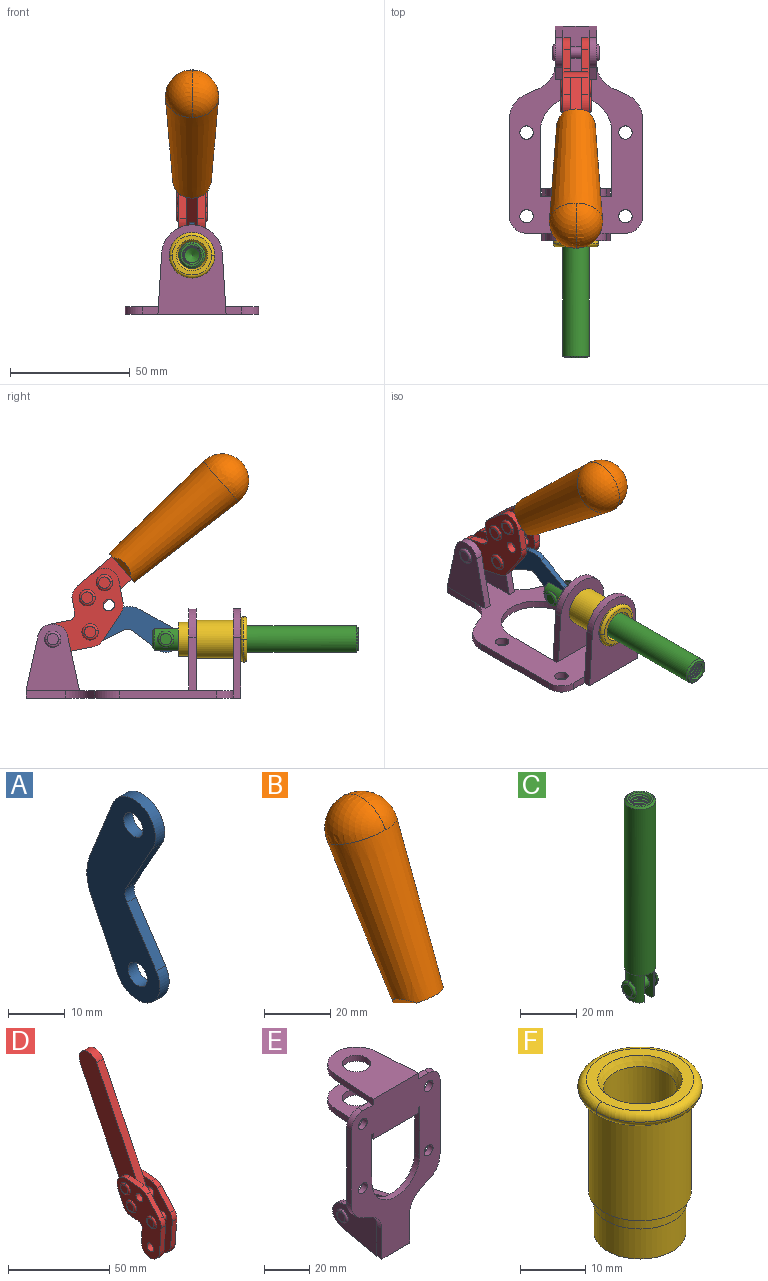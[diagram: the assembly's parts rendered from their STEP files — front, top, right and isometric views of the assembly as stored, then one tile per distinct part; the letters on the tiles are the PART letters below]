
ASSEMBLY  parts=6 mates=6
PART A: 12 faces, bbox 2.3x18.2x42.8 mm
  f0: cylinder r=2.4mm len=4.8mm, axis (1,0,0), area 34.9mm2, adj f4,f11
  f1: cylinder r=10.41mm len=8.47mm, axis (1,0,0), area 20.2mm2, adj f4,f9,f10,f11
  f2: cylinder r=3.05mm len=3.16mm, axis (1,0,0), area 7.7mm2, adj f4,f6,f7,f11
  f3: cylinder r=2.4mm len=4.8mm, axis (1,0,0), area 34.9mm2, adj f4,f11
  f4: plane 42.81x18.23mm, normal (-1,0,0), area 414.1mm2, adj f0,f1,f2,f3,f5,f6,f7,f8
  f5: cylinder r=5.54mm len=10.67mm, axis (1,0,0), area 41.8mm2, adj f4,f6,f10,f11
  f6: plane 11.66x6.53mm, normal (0,-0.87,-0.49), area 30.9mm2, adj f2,f4,f5,f11
  f7: plane 11.17x7.33mm, normal (0,-0.84,0.55), area 30.9mm2, adj f2,f4,f8,f11
  f8: cylinder r=5.54mm len=10.51mm, axis (1,0,0), area 41.8mm2, adj f4,f7,f9,f11
  f9: plane 13.67x6.67mm, normal (0,0.9,-0.44), area 35.1mm2, adj f1,f4,f8,f11
  f10: plane 14.1x5.7mm, normal (0,0.93,0.37), area 35.1mm2, adj f1,f4,f5,f11
  f11: plane 42.81x18.23mm, normal (1,0,0), area 414.1mm2, adj f0,f1,f2,f3,f5,f6,f7,f8
PART B: 11 faces, bbox 22.3x42.6x64.5 mm
  f0: sphere r=11.13mm, area 411.4mm2, adj f1,f8
  f1: cone r=11.11mm half-angle=3.3deg, axis (0,0.44,0.9), area 3251.8mm2, adj f0,f7,f8,f9,f10
  f2: cylinder r=6.16mm len=11.7mm, axis (1,0,0), area 89.5mm2, adj f3,f4,f5,f6
  f3: plane 60.23x36.75mm, normal (-1,0,0), area 763.6mm2, adj f2,f4,f6,f10
  f4: plane 51.37x25.05mm, normal (0,0.9,-0.44), area 264.2mm2, adj f2,f3,f5,f10
  f5: plane 60.23x36.75mm, normal (1,0,0), area 763.6mm2, adj f2,f4,f6,f10
  f6: plane 51.37x25.05mm, normal (0,-0.9,0.44), area 264.2mm2, adj f2,f3,f5,f10
  f7: plane 9.95x5.95mm, normal (0.71,-0.31,-0.64), area 25.8mm2, adj f1,f10
  f8: sphere r=11.13mm, area 411.4mm2, adj f0,f1
  f9: plane 9.95x5.95mm, normal (-0.71,-0.31,-0.64), area 25.8mm2, adj f1,f10
  f10: plane 14.27x11.38mm, normal (0,-0.44,-0.9), area 106.7mm2, adj f1,f3,f4,f5,f6,f7,f9
PART C: 48 faces, bbox 12.6x11.1x86.1 mm
  f0: torus R=2.41mm, axis (-1,0,0), area 15mm2, adj f30,f32,f34
  f1: torus R=2.41mm, axis (-1,0,0), area 15mm2, adj f29,f31,f33
  f2: cylinder r=5.54mm len=72.39mm, axis (0,0,1), area 2518.5mm2, adj f3,f4,f42,f43
  f3: cone r=5.54mm half-angle=45deg, axis (0,0,1), area 7.6mm2, adj f2,f5,f41
  f4: cone r=5.54mm half-angle=45deg, axis (0,0,-1), area 34.9mm2, adj f2,f39
  f5: cylinder r=5.08mm len=11.48mm, axis (0,0,1), area 108.3mm2, adj f3,f7,f8,f41
  f6: cylinder r=2.41mm len=4.83mm, axis (-1,0,0), area 71.2mm2, adj f40,f41
  f7: cylinder r=2.41mm len=4.83mm, axis (-1,0,0), area 7.6mm2, adj f5,f34
  f8: cone r=5.08mm half-angle=45deg, axis (0,0,1), area 10.6mm2, adj f5,f37,f41
  f9: cone r=3.98mm half-angle=45deg, axis (0,0,1), area 17.6mm2, adj f27,f39,f45,f46,f47
  f10: cylinder r=2.41mm len=4.83mm, axis (-1,0,0), area 7.6mm2, adj f33,f38
  f11: cylinder r=3.2mm len=6.4mm, axis (0,0,1), area 78.4mm2, adj f12,f28,f44,f45,f47
  f12: cylinder r=3.2mm len=6.4mm, axis (0,0,1), area 10.5mm2, adj f11,f13,f45,f47
  f13: cylinder r=3.2mm len=6.4mm, axis (0,0,1), area 10.5mm2, adj f12,f14,f45,f47
  f14: cylinder r=3.2mm len=6.4mm, axis (0,0,1), area 10.5mm2, adj f13,f15,f45,f47
  f15: cylinder r=3.2mm len=6.4mm, axis (0,0,1), area 10.5mm2, adj f14,f16,f45,f47
  f16: cylinder r=3.2mm len=6.4mm, axis (0,0,1), area 10.5mm2, adj f15,f17,f45,f47
  f17: cylinder r=3.2mm len=6.4mm, axis (0,0,1), area 10.5mm2, adj f16,f18,f45,f47
  f18: cylinder r=3.2mm len=6.4mm, axis (0,0,1), area 10.5mm2, adj f17,f19,f45,f47
  f19: cylinder r=3.2mm len=6.4mm, axis (0,0,1), area 10.5mm2, adj f18,f20,f45,f47
  f20: cylinder r=3.2mm len=6.4mm, axis (0,0,1), area 10.5mm2, adj f19,f21,f45,f47
  f21: cylinder r=3.2mm len=6.4mm, axis (0,0,1), area 10.5mm2, adj f20,f22,f45,f47
  f22: cylinder r=3.2mm len=6.4mm, axis (0,0,1), area 10.5mm2, adj f21,f23,f45,f47
  f23: cylinder r=3.2mm len=6.4mm, axis (0,0,1), area 10.5mm2, adj f22,f24,f45,f47
  f24: cylinder r=3.2mm len=6.4mm, axis (0,0,1), area 10.5mm2, adj f23,f25,f45,f47
  f25: cylinder r=3.2mm len=6.4mm, axis (0,0,1), area 10.5mm2, adj f24,f26,f45,f47
  f26: cylinder r=3.2mm len=6.4mm, axis (0,0,1), area 10.5mm2, adj f25,f27,f45,f47
  f27: cylinder r=3.2mm len=6.4mm, axis (0,0,1), area 7.4mm2, adj f9,f26,f45,f47
  f28: cone r=3.2mm half-angle=60deg, axis (0,0,1), area 37.2mm2, adj f11
  f29: plane 4.83x4.83mm, normal (-1,0,0), area 18.3mm2, adj f1,f31
  f30: plane 4.83x4.83mm, normal (1,0,0), area 18.3mm2, adj f0,f32
  f31: torus R=2.41mm, axis (-1,0,0), area 15mm2, adj f1,f29,f33
  f32: torus R=2.41mm, axis (-1,0,0), area 15mm2, adj f0,f30,f34
  f33: plane 6.83x6.83mm, normal (1,0,0), area 18.3mm2, adj f1,f10,f31
  f34: plane 6.83x6.83mm, normal (-1,0,0), area 18.3mm2, adj f0,f7,f32
  f35: cone r=5.08mm half-angle=45deg, axis (0,0,1), area 10.6mm2, adj f36,f38,f40
  f36: plane 7.25x1.97mm, normal (0,0,-1), area 10mm2, adj f35,f40
  f37: plane 7.25x1.97mm, normal (0,0,-1), area 10mm2, adj f8,f41
  f38: cylinder r=5.08mm len=11.48mm, axis (0,0,1), area 108.3mm2, adj f10,f35,f40,f42
  f39: plane 9.55x9.55mm, normal (0,0,1), area 22mm2, adj f4,f9
  f40: plane 12.76x10.09mm, normal (1,0,0), area 95.7mm2, adj f6,f35,f36,f38,f42,f43
  f41: plane 12.76x10.09mm, normal (-1,0,0), area 95.7mm2, adj f3,f5,f6,f8,f37,f43
  f42: cone r=5.54mm half-angle=45deg, axis (0,0,1), area 7.6mm2, adj f2,f38,f40
  f43: plane 11.07x4.7mm, normal (0,0,-1), area 50.4mm2, adj f2,f40,f41
  f44: plane 0.89x0.62mm, normal (-1,0,0), area 0.3mm2, adj f11,f45,f46,f47
  f45: bspline ~24.8x7.63mm, area 266.6mm2, adj f9,f11,f12,f13,f14,f15,f16,f17
  f46: bspline ~24.87x7.63mm, area 73.6mm2, adj f9,f44,f45,f47
  f47: bspline ~24.98x7.63mm, area 272.5mm2, adj f9,f11,f12,f13,f14,f15,f16,f17
PART D: 59 faces, bbox 12.9x60.2x99.6 mm
  f0: torus R=2.39mm, axis (-1,0,0), area 14.9mm2, adj f20,f43,f51
  f1: torus R=2.39mm, axis (-1,0,0), area 14.9mm2, adj f19,f42,f51
  f2: torus R=2.39mm, axis (-1,0,0), area 14.9mm2, adj f18,f35,f51
  f3: torus R=2.39mm, axis (-1,0,0), area 14.9mm2, adj f14,f17,f23
  f4: torus R=2.39mm, axis (-1,0,0), area 14.9mm2, adj f13,f16,f23
  f5: torus R=2.39mm, axis (-1,0,0), area 14.9mm2, adj f12,f15,f23
  f6: cylinder r=2.39mm len=4.78mm, axis (1,0,0), area 46.5mm2, adj f48,f50,f51
  f7: cylinder r=2.39mm len=4.78mm, axis (1,0,0), area 46.5mm2, adj f50,f51
  f8: cylinder r=6.35mm len=12.68mm, axis (1,0,0), area 61.8mm2, adj f38,f39,f50,f51
  f9: cylinder r=2.39mm len=4.78mm, axis (-1,0,0), area 70.5mm2, adj f46,f50
  f10: cylinder r=2.39mm len=4.78mm, axis (-1,0,0), area 46.5mm2, adj f23,f45,f46
  f11: cylinder r=2.39mm len=4.78mm, axis (-1,0,0), area 46.5mm2, adj f23,f46
  f12: plane 4.78x4.78mm, normal (1,0,0), area 17.9mm2, adj f5,f15
  f13: plane 4.78x4.78mm, normal (1,0,0), area 17.9mm2, adj f4,f16
  f14: plane 4.78x4.78mm, normal (1,0,0), area 17.9mm2, adj f3,f17
  f15: torus R=2.39mm, axis (-1,0,0), area 14.9mm2, adj f5,f12,f23
  f16: torus R=2.39mm, axis (-1,0,0), area 14.9mm2, adj f4,f13,f23
  f17: torus R=2.39mm, axis (-1,0,0), area 14.9mm2, adj f3,f14,f23
  f18: plane 4.78x4.78mm, normal (-1,0,0), area 17.9mm2, adj f2,f35
  f19: plane 4.78x4.78mm, normal (-1,0,0), area 17.9mm2, adj f1,f42
  f20: plane 4.78x4.78mm, normal (-1,0,0), area 17.9mm2, adj f0,f43
  f21: plane 2.26x0.2mm, normal (1,0,0), area 0.2mm2, adj f31,f44
  f22: plane 2.26x0.2mm, normal (-1,0,0), area 0.2mm2, adj f41,f44
  f23: plane 39.37x30.77mm, normal (1,0,0), area 565.5mm2, adj f3,f4,f5,f10,f11,f15,f16,f17
  f24: cylinder r=6.1mm len=4.15mm, axis (-1,0,0), area 14.7mm2, adj f23,f25,f32,f46
  f25: plane 10.25x9.01mm, normal (0,-0.75,0.66), area 42.3mm2, adj f23,f24,f26,f46
  f26: cylinder r=6.35mm len=4.64mm, axis (-1,0,0), area 15.6mm2, adj f23,f25,f27,f46
  f27: plane 15.84x3.1mm, normal (0,-1,-0.07), area 49.2mm2, adj f23,f26,f28,f46
  f28: cylinder r=6.35mm len=12.68mm, axis (-1,0,0), area 61.8mm2, adj f23,f27,f29,f46
  f29: plane 8.11x3.1mm, normal (0,1,0.07), area 25.2mm2, adj f23,f28,f30,f46
  f30: cylinder r=3.05mm len=3.25mm, axis (-1,0,0), area 14.8mm2, adj f23,f29,f31,f46
  f31: plane 5.99x3.1mm, normal (0,0.07,-1), area 18.6mm2, adj f21,f23,f30,f44,f46
  f32: plane 9.5x3.1mm, normal (0,-0.07,1), area 29.5mm2, adj f23,f24,f33,f46,f47
  f33: cylinder r=6.1mm len=8.63mm, axis (-1,0,0), area 39.1mm2, adj f23,f32,f34,f47
  f34: plane 8.65x3.96mm, normal (0,0.91,-0.42), area 29.5mm2, adj f23,f33,f44,f47
  f35: torus R=2.39mm, axis (-1,0,0), area 14.9mm2, adj f2,f18,f51
  f36: plane 10.25x9.01mm, normal (0,-0.75,0.66), area 42.3mm2, adj f37,f49,f50,f51
  f37: cylinder r=6.35mm len=4.64mm, axis (1,0,0), area 15.6mm2, adj f36,f38,f50,f51
  f38: plane 15.84x3.1mm, normal (0,-1,-0.07), area 49.2mm2, adj f8,f37,f50,f51
  f39: plane 8.11x3.1mm, normal (0,1,0.07), area 25.2mm2, adj f8,f40,f50,f51
  f40: cylinder r=3.05mm len=3.25mm, axis (1,0,0), area 14.8mm2, adj f39,f41,f50,f51
  f41: plane 5.99x3.1mm, normal (0,0.07,-1), area 18.6mm2, adj f22,f40,f44,f50,f51
  f42: torus R=2.39mm, axis (-1,0,0), area 14.9mm2, adj f1,f19,f51
  f43: torus R=2.39mm, axis (-1,0,0), area 14.9mm2, adj f0,f20,f51
  f44: cylinder r=6.35mm len=12.12mm, axis (-1,0,0), area 128.9mm2, adj f21,f22,f23,f31,f34,f41,f46,f47
  f45: plane 2.65x1.35mm, normal (1,0,0), area 1mm2, adj f10,f55
  f46: plane 39.08x20.42mm, normal (-1,0,0), area 412.5mm2, adj f9,f10,f11,f24,f25,f26,f27,f28
  f47: plane 77.62x39.82mm, normal (1,0,0), area 850mm2, adj f32,f33,f34,f44,f53,f54,f55
  f48: plane 2.65x1.35mm, normal (-1,0,0), area 1mm2, adj f6,f55
  f49: cylinder r=6.1mm len=4.15mm, axis (1,0,0), area 14.7mm2, adj f36,f50,f51,f56
  f50: plane 39.08x20.42mm, normal (1,0,0), area 412.5mm2, adj f6,f7,f8,f9,f36,f37,f38,f39
  f51: plane 39.37x30.77mm, normal (-1,0,0), area 565.5mm2, adj f0,f1,f2,f6,f7,f8,f35,f36
  f52: plane 8.65x3.96mm, normal (0,0.91,-0.42), area 29.5mm2, adj f44,f51,f57,f58
  f53: plane 68.49x33.4mm, normal (0,0.9,-0.44), area 358.1mm2, adj f44,f47,f54,f58
  f54: cylinder r=6.35mm len=12.06mm, axis (1,0,0), area 93.7mm2, adj f47,f53,f55,f58
  f55: plane 68.49x33.4mm, normal (0,-0.9,0.44), area 358.1mm2, adj f44,f45,f46,f47,f48,f50,f54,f58
  f56: plane 9.5x3.1mm, normal (0,-0.07,1), area 29.5mm2, adj f49,f50,f51,f57,f58
  f57: cylinder r=6.1mm len=8.63mm, axis (1,0,0), area 39.1mm2, adj f51,f52,f56,f58
  f58: plane 77.62x39.82mm, normal (-1,0,0), area 850mm2, adj f44,f52,f53,f54,f55,f56,f57
PART E: 55 faces, bbox 55.7x37.4x89.8 mm
  f0: torus R=2.41mm, axis (-1,0,0), area 15mm2, adj f11,f15,f25
  f1: torus R=2.41mm, axis (-1,0,0), area 15mm2, adj f10,f12,f22
  f2: cylinder r=2.78mm len=5.56mm, axis (0,-1,0), area 54.2mm2, adj f30,f54
  f3: cylinder r=14.99mm len=29.97mm, axis (0,-1,0), area 145.9mm2, adj f30,f49,f53,f54
  f4: cylinder r=2.78mm len=5.56mm, axis (0,-1,0), area 54.2mm2, adj f30,f54
  f5: cylinder r=2.78mm len=5.56mm, axis (0,-1,0), area 54.2mm2, adj f30,f54
  f6: cylinder r=2.78mm len=5.56mm, axis (0,-1,0), area 54.2mm2, adj f30,f54
  f7: cylinder r=6.35mm len=12.7mm, axis (0,0,1), area 123.6mm2, adj f27,f51
  f8: cylinder r=6.35mm len=12.7mm, axis (0,0,-1), area 124.7mm2, adj f21,f35
  f9: cylinder r=2.41mm len=11.18mm, axis (-1,0,0), area 169.4mm2, adj f16,f19
  f10: plane 4.83x4.83mm, normal (1,0,0), area 18.3mm2, adj f1,f12
  f11: plane 4.83x4.83mm, normal (-1,0,0), area 18.3mm2, adj f0,f15
  f12: torus R=2.41mm, axis (-1,0,0), area 15mm2, adj f1,f10,f22
  f13: cylinder r=6.35mm len=12.41mm, axis (1,0,0), area 53.4mm2, adj f18,f19,f22,f23
  f14: cylinder r=6.35mm len=12.41mm, axis (-1,0,0), area 53.4mm2, adj f16,f17,f24,f25
  f15: torus R=2.41mm, axis (-1,0,0), area 15mm2, adj f0,f11,f25
  f16: plane 27.86x22.35mm, normal (1,0,0), area 425.4mm2, adj f9,f14,f17,f24,f30
  f17: plane 22.86x4.97mm, normal (0,0.21,0.98), area 72.5mm2, adj f14,f16,f25,f30
  f18: plane 22.86x4.97mm, normal (0,0.21,0.98), area 72.5mm2, adj f13,f19,f22,f30
  f19: plane 27.86x22.35mm, normal (-1,0,0), area 425.4mm2, adj f9,f13,f18,f23,f30
  f20: cylinder r=12.7mm len=25.35mm, axis (0,0,-1), area 119.8mm2, adj f21,f34,f35,f36
  f21: plane 34.21x28.07mm, normal (0,0,-1), area 702.4mm2, adj f8,f20,f30,f34,f36
  f22: plane 27.96x22.45mm, normal (1,0,0), area 407.2mm2, adj f1,f12,f13,f18,f23,f30,f42,f43
  f23: plane 22.86x4.97mm, normal (0,0.21,-0.98), area 72.5mm2, adj f13,f19,f22,f44
  f24: plane 22.86x4.97mm, normal (0,0.21,-0.98), area 72.5mm2, adj f14,f16,f25,f44
  f25: plane 27.86x22.35mm, normal (-1,0,0), area 407.1mm2, adj f0,f14,f15,f17,f24,f30,f45,f46
  f26: plane 3.1x0.95mm, normal (0,0,-1), area 2.7mm2, adj f30,f49,f50,f54
  f27: plane 34.21x28.07mm, normal (0,0,1), area 702.4mm2, adj f7,f28,f30,f50,f52
  f28: cylinder r=12.7mm len=25.35mm, axis (0,0,1), area 118.8mm2, adj f27,f50,f51,f52
  f29: plane 3.1x0.95mm, normal (0,0,-1), area 2.7mm2, adj f30,f52,f53,f54
  f30: plane 86.54x55.63mm, normal (0,1,0), area 2362.9mm2, adj f2,f3,f4,f5,f6,f16,f17,f18
  f31: plane 40.56x3.1mm, normal (-1,0,0), area 125.7mm2, adj f30,f32,f48,f54
  f32: cylinder r=7.11mm len=7.11mm, axis (0,-1,0), area 34.6mm2, adj f30,f31,f33,f54
  f33: plane 6.67x3.1mm, normal (0,0,1), area 20.4mm2, adj f30,f32,f34,f54
  f34: plane 25.39x3.13mm, normal (-1,0.06,0), area 79.5mm2, adj f20,f21,f33,f35,f54
  f35: plane 37.31x28.45mm, normal (0,0,1), area 789.9mm2, adj f8,f20,f34,f36,f54
  f36: plane 25.39x3.13mm, normal (1,0.06,0), area 79.5mm2, adj f20,f21,f35,f37,f54
  f37: plane 6.67x3.1mm, normal (0,0,1), area 20.4mm2, adj f30,f36,f38,f54
  f38: cylinder r=7.11mm len=7.11mm, axis (0,-1,0), area 34.6mm2, adj f30,f37,f39,f54
  f39: plane 40.56x3.1mm, normal (1,0,0), area 125.7mm2, adj f30,f38,f40,f54
  f40: cylinder r=11.18mm len=10.16mm, axis (0,-1,0), area 39.5mm2, adj f30,f39,f41,f54
  f41: plane 6.09x3.1mm, normal (0.42,0,-0.91), area 20.8mm2, adj f30,f40,f42,f54
  f42: cylinder r=11.18mm len=9.41mm, axis (0,-1,0), area 37.2mm2, adj f22,f30,f41,f43,f54
  f43: plane 16.5x3.1mm, normal (1,0,0), area 51.1mm2, adj f22,f42,f44,f54
  f44: plane 17.37x3.1mm, normal (0,0,-1), area 53.8mm2, adj f23,f24,f30,f43,f45,f54
  f45: plane 16.5x3.1mm, normal (-1,0,0), area 51.1mm2, adj f25,f44,f46,f54
  f46: cylinder r=11.18mm len=9.41mm, axis (0,-1,0), area 37.2mm2, adj f25,f30,f45,f47,f54
  f47: plane 6.09x3.1mm, normal (-0.42,0,-0.91), area 20.8mm2, adj f30,f46,f48,f54
  f48: cylinder r=11.18mm len=10.16mm, axis (0,-1,0), area 39.5mm2, adj f30,f31,f47,f54
  f49: plane 26.54x3.1mm, normal (-1,0,0), area 82.3mm2, adj f3,f26,f30,f54
  f50: plane 25.39x3.1mm, normal (1,0.06,0), area 78.8mm2, adj f26,f27,f28,f51,f54
  f51: plane 37.31x28.45mm, normal (0,0,-1), area 789.9mm2, adj f7,f28,f50,f52,f54
  f52: plane 25.39x3.1mm, normal (-1,0.06,0), area 78.8mm2, adj f27,f28,f29,f51,f54
  f53: plane 26.54x3.1mm, normal (1,0,0), area 82.3mm2, adj f3,f29,f30,f54
  f54: plane 89.66x55.63mm, normal (0,-1,0), area 2678.5mm2, adj f2,f3,f4,f5,f6,f26,f29,f31
PART F: 15 faces, bbox 20.6x20.6x28.7 mm
  f0: torus R=8.26mm, axis (0,0,1), area 56.8mm2, adj f1,f10,f12
  f1: torus R=8.26mm, axis (0,0,1), area 56.8mm2, adj f0,f6,f13
  f2: cylinder r=5.59mm len=25.91mm, axis (0,0,1), area 909.6mm2, adj f3,f4
  f3: cone r=6.86mm half-angle=45deg, axis (0,0,-1), area 70.2mm2, adj f2,f14
  f4: cone r=6.47mm half-angle=30deg, axis (0,0,1), area 66.7mm2, adj f2,f13
  f5: cylinder r=7.04mm len=14.07mm, axis (0,0,1), area 252.6mm2, adj f11,f14
  f6: torus R=8.26mm, axis (0,0,1), area 56.8mm2, adj f1,f12,f13
  f7: cylinder r=7.16mm len=14.33mm, axis (0,0,1), area 91.5mm2, adj f9,f11
  f8: cylinder r=7.86mm len=18.42mm, axis (0,0,1), area 909.6mm2, adj f9,f10
  f9: plane 15.72x15.72mm, normal (0,0,-1), area 33mm2, adj f7,f8
  f10: plane 16.51x16.51mm, normal (0,0,-1), area 19.9mm2, adj f0,f8,f12
  f11: plane 14.33x14.33mm, normal (0,0,-1), area 5.7mm2, adj f5,f7
  f12: torus R=8.26mm, axis (0,0,1), area 56.8mm2, adj f0,f6,f10
  f13: plane 16.51x16.51mm, normal (0,0,1), area 82.7mm2, adj f1,f4,f6
  f14: plane 14.07x14.07mm, normal (0,0,-1), area 7.8mm2, adj f3,f5
PLACE A rot(axis=(0,-0.69,-0.73),180deg) t=(0,11.7,2.14)mm
PLACE B rot(axis=(1,0,0),75deg) t=(0,3.86,9.14)mm
PLACE C rot(axis=(1,0,0),90deg) t=(0,9.52,0)mm
PLACE D rot(axis=(1,0,0),75deg) t=(0,3.86,9.14)mm
PLACE E rot(axis=(1,0,0),90deg) t=(0,9.14,0)mm fixed
PLACE F rot(axis=(1,0,0),90deg) t=(0,9.14,0)mm
MATE slider C.f2 <-> E.f7  axis (0,-1,0) through (0,-49.26,24.61)mm
MATE revolute A.f5 <-> D.f4  axis (-1,0,0) through (0,25.65,27.64)mm
MATE revolute D.f7 <-> E.f0  axis (1,0,0) through (0,41.23,24.61)mm
MATE fastened B.f2 <-> D.f54  axis (1,0,0) through (0,-30.66,91.94)mm
MATE fastened F.f0 <-> E.f7  axis (0,1,0) through (0,-37.25,24.61)mm
MATE revolute A.f3 <-> C.f6  axis (-1,0,0) through (0,-5.96,24.61)mm
